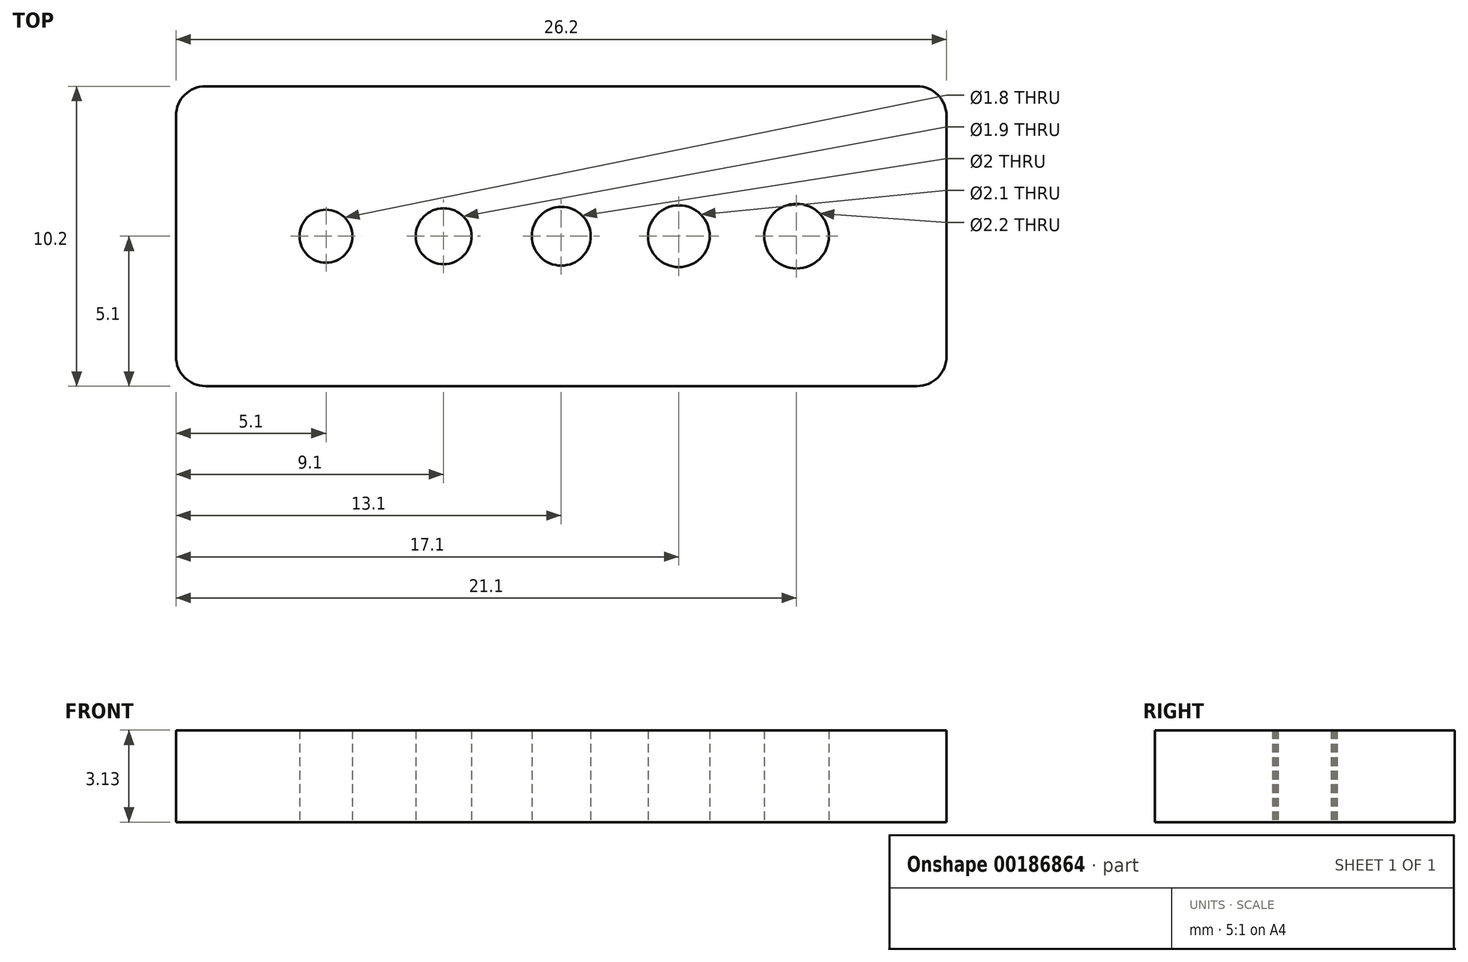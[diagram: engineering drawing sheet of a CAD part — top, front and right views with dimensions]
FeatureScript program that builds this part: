
annotation { "Feature Type Name" : "Feature", "Feature Type Description" : "" }
export const myFeature = defineFeature(function(context is Context, id is Id, definition is map)
    precondition{}
    {
        {
            var Q0;
            Q0=qCreatedBy(makeId("Top.planeOp"),FACE);
            var sketch = newSketch(context, id + "F0", { "sketchPlane" : qUnion([Q0])});
            skLineSegment(sketch, "E0.bottom", {"start": v(12.1, -5.1) * mm, "end": v(-12.1, -5.1) * mm});
            skLineSegment(sketch, "E0.top", {"start": v(12.1, 5.1) * mm, "end": v(-12.1, 5.1) * mm});
            skLineSegment(sketch, "E0.left", {"start": v(13.1, -4.1) * mm, "end": v(13.1, 4.1) * mm});
            skLineSegment(sketch, "E0.right", {"start": v(-13.1, -4.1) * mm, "end": v(-13.1, 4.1) * mm});
            skPoint(sketch, "E0.middle", {"position": v(0, 0) * mm});
            skCircle(sketch, "E1", {"center": v(-8, 0) * mm, "radius": 0.9 * mm});
            skCircle(sketch, "E2", {"center": v(-4, 0) * mm, "radius": 0.95 * mm});
            skCircle(sketch, "E3", {"center": v(0, 0) * mm, "radius": 1 * mm});
            skCircle(sketch, "E4", {"center": v(4, 0) * mm, "radius": 1.05 * mm});
            skCircle(sketch, "E5", {"center": v(8, 0) * mm, "radius": 1.1 * mm});
            skLineSegment(sketch, "E6", {"start": v(-8, 0) * mm, "end": v(-4, 0) * mm, "construction": true});
            skLineSegment(sketch, "E7", {"start": v(0, 0) * mm, "end": v(-4, 0) * mm, "construction": true});
            skLineSegment(sketch, "E8", {"start": v(4, 0) * mm, "end": v(0, 0) * mm, "construction": true});
            skLineSegment(sketch, "E9", {"start": v(8, 0) * mm, "end": v(4, 0) * mm, "construction": true});
            skPoint(sketch, "E10.visualSharp", {"position": v(-13.1, 5.1) * mm});
            skArc(sketch, "E10.filletArc", {"start": v(-12.1, 5.1) * mm, "mid": v(-12.8, 4.8) * mm, "end": v(-13.1, 4.1) * mm});
            skPoint(sketch, "E11.visualSharp", {"position": v(-13.1, -5.1) * mm});
            skArc(sketch, "E11.filletArc", {"start": v(-13.1, -4.1) * mm, "mid": v(-12.8, -4.8) * mm, "end": v(-12.1, -5.1) * mm});
            skPoint(sketch, "E12.visualSharp", {"position": v(13.1, -5.1) * mm});
            skArc(sketch, "E12.filletArc", {"start": v(12.1, -5.1) * mm, "mid": v(12.8, -4.8) * mm, "end": v(13.1, -4.1) * mm});
            skPoint(sketch, "E13.visualSharp", {"position": v(13.1, 5.1) * mm});
            skArc(sketch, "E13.filletArc", {"start": v(13.1, 4.1) * mm, "mid": v(12.8, 4.8) * mm, "end": v(12.1, 5.1) * mm});
            skSolve(sketch);
        }
        {
            var Q0;
            Q0 = qSketchRegion(id + "F0", true);
            extrude(context, id + "F1", {"entities" : qUnion([Q0]), "depth" : 3.12 * mm});
        }
    });
